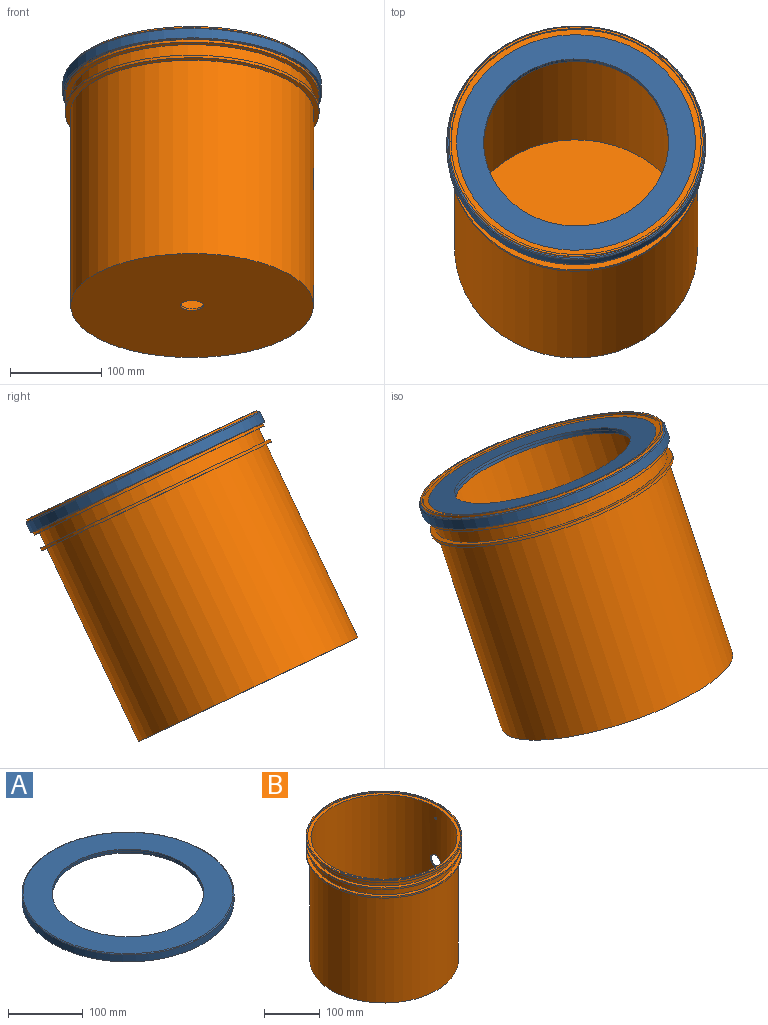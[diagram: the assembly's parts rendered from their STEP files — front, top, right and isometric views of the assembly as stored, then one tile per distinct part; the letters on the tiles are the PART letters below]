
ASSEMBLY  parts=2 mates=1
PART A: 8 faces, bbox 307.9x307.9x12.7 mm
  f0: plane 284.48x284.48mm, normal (0,0,-1), area 1803.1mm2, adj f1,f6
  f1: cylinder r=142.24mm len=284.48mm, axis (0,0,-1), area 10215.2mm2, adj f0,f2
  f2: torus R=140.97mm, axis (0,0,-1), area 1777.1mm2, adj f1,f3
  f3: plane 281.94x281.94mm, normal (0,0,1), area 30002.1mm2, adj f2,f7
  f4: cone r=102.11mm half-angle=9.7deg, axis (0,0,1), area 1929mm2, adj f5,f7
  f5: plane 280.42x280.42mm, normal (0,0,-1), area 29003.9mm2, adj f4,f6
  f6: cylinder r=140.21mm len=280.42mm, axis (0,0,-1), area 8391.1mm2, adj f0,f5
  f7: cylinder r=101.6mm len=203.2mm, axis (0,0,1), area 3923.5mm2, adj f3,f4
PART B: 20 faces, bbox 279.4x279.4x273.1 mm
  f0: cylinder r=133.35mm len=266.7mm, axis (0,0,1), area 196348.5mm2, adj f10,f11,f17
  f1: cylinder r=131.11mm len=268.42mm, axis (0,0,1), area 220608.5mm2, adj f14,f16,f17,f19
  f2: cylinder r=133.35mm len=266.7mm, axis (0,0,1), area 13286.6mm2, adj f3,f13,f19
  f3: plane 279.4x279.4mm, normal (0,0,-1), area 5447.1mm2, adj f2,f4
  f4: cylinder r=139.7mm len=279.4mm, axis (0,0,1), area 2786.9mm2, adj f3,f5
  f5: plane 279.4x279.4mm, normal (0,0,1), area 5447.1mm2, adj f4,f6
  f6: cylinder r=133.35mm len=266.7mm, axis (0,0,1), area 9422.8mm2, adj f5,f7
  f7: plane 279.4x279.4mm, normal (0,0,-1), area 5447.1mm2, adj f6,f8
  f8: cylinder r=139.7mm len=279.4mm, axis (0,0,1), area 4062.9mm2, adj f7,f9
  f9: plane 279.4x279.4mm, normal (0,0,1), area 1946.3mm2, adj f8,f15
  f10: plane 266.7x266.7mm, normal (0,0,-1), area 55357.8mm2, adj f0,f18
  f11: plane 279.4x279.4mm, normal (0,0,-1), area 5447.1mm2, adj f0,f12
  f12: cylinder r=139.7mm len=279.4mm, axis (0,0,1), area 2786.9mm2, adj f11,f13
  f13: plane 279.4x279.4mm, normal (0,0,1), area 5447.1mm2, adj f2,f12
  f14: plane 274.93x274.93mm, normal (0,0,1), area 5357.9mm2, adj f1,f15
  f15: cylinder r=137.46mm len=274.93mm, axis (0,0,1), area 2067.3mm2, adj f9,f14
  f16: plane 262.23x262.23mm, normal (0,0,1), area 53500.7mm2, adj f1,f18
  f17: cylinder r=12.7mm len=25.4mm, axis (-1,0,0), area 178.8mm2, adj f0,f1
  f18: cylinder r=12.7mm len=25.4mm, axis (0,0,-1), area 178.4mm2, adj f10,f16
  f19: cylinder r=2.14mm len=4.28mm, axis (1,0,0), area 30.1mm2, adj f1,f2
PLACE A rot(axis=(-1,0,0),25.4deg) t=(45.16,-8.9,154.24)mm
PLACE B rot(axis=(-1,0,0),25.4deg) t=(45.16,-69.99,25.41)mm
MATE fastened A.f1 <-> B.f0  axis (0,0.43,0.9) through (45.16,-8.9,154.24)mm
